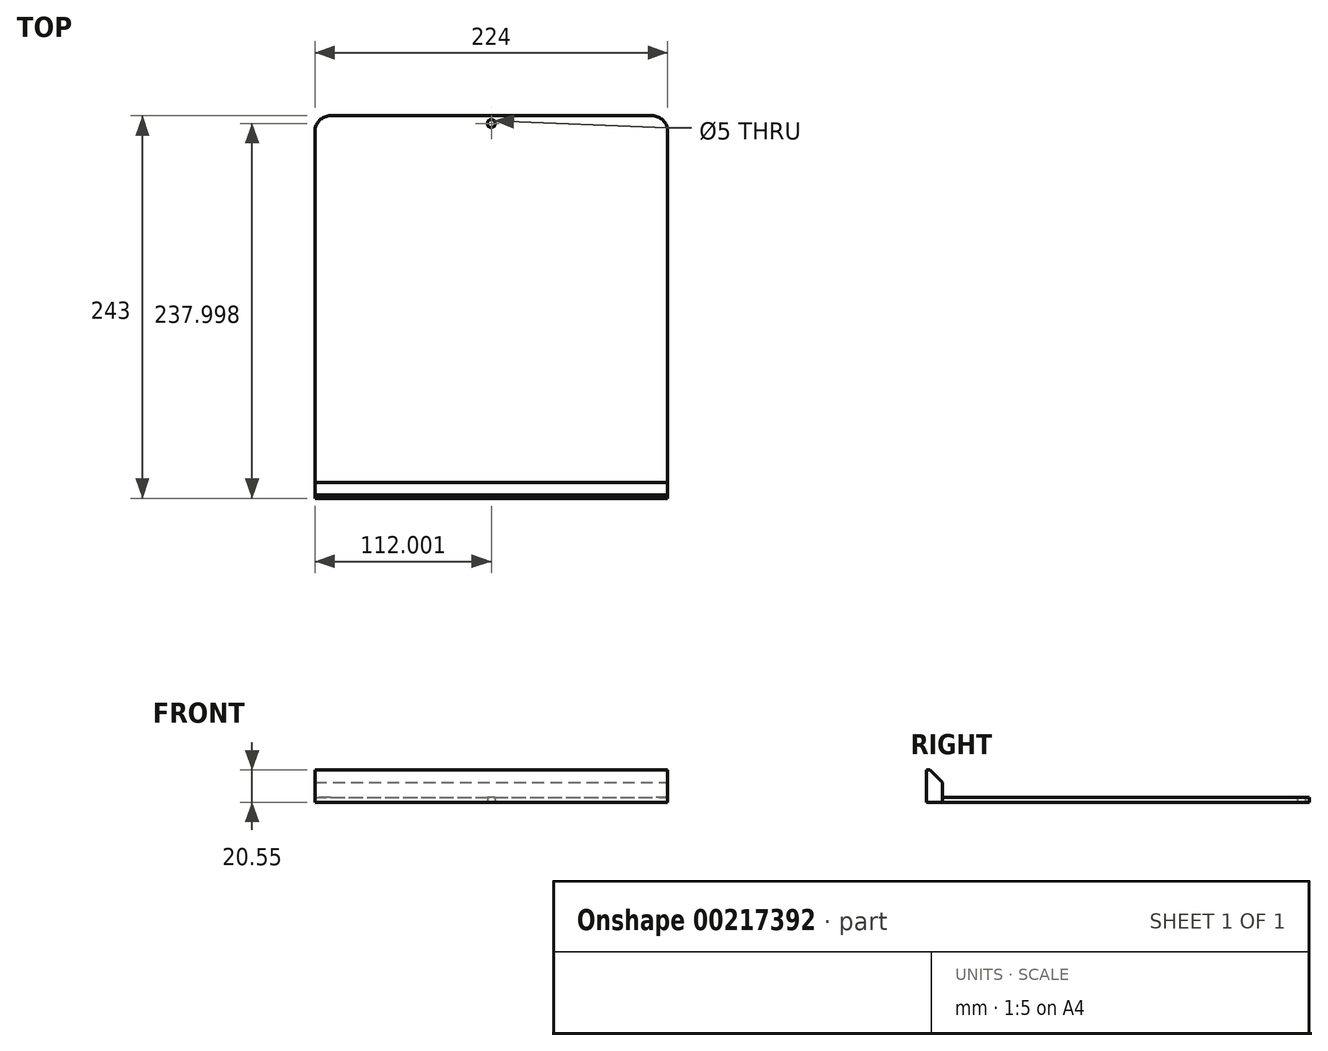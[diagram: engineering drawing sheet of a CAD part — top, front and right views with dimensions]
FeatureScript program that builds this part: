
annotation { "Feature Type Name" : "Feature", "Feature Type Description" : "" }
export const myFeature = defineFeature(function(context is Context, id is Id, definition is map)
    precondition{}
    {
        {
            var Q0;
            Q0=qCreatedBy(makeId("Top.planeOp"),FACE);
            var sketch = newSketch(context, id + "F0", { "sketchPlane" : qUnion([Q0])});
            skLineSegment(sketch, "E0.bottom", {"start": v(-146.57, -160.81) * mm, "end": v(77.43, -160.81) * mm});
            skLineSegment(sketch, "E0.top", {"start": v(-146.57, 72.19) * mm, "end": v(77.43, 72.19) * mm});
            skLineSegment(sketch, "E0.left", {"start": v(-146.57, -160.81) * mm, "end": v(-146.57, 72.19) * mm});
            skLineSegment(sketch, "E0.right", {"start": v(77.43, -160.81) * mm, "end": v(77.43, 72.19) * mm});
            skCircle(sketch, "E1", {"center": v(-34.57, 67.19) * mm, "radius": 2.5 * mm});
            skSolve(sketch);
        }
        {
            var Q0;
            Q0=makeQuery(id+"F0.imprint","IMPRINT",FACE,{"disambiguationData":[TD([[makeQuery(id+"F0.imprint","IMPRINT",EDGE,{"derivedFrom":sQuery(id+"F0.wireOp",EDGE,"E0.bottom")}),1.0]])]});
            extrude(context, id + "F1", {"entities" : qUnion([Q0]), "depth" : 3 * mm});
        }
        {
            var Q0;
            Q0=makeQuery(id+"F1.opExtrude","SWEPT_FACE",FACE,{"disambiguationData":[OSD([sQuery(id+"F0.wireOp",EDGE,"E0.bottom")])]});
            var sketch = newSketch(context, id + "F2", { "sketchPlane" : qUnion([Q0])});
            skLineSegment(sketch, "E2.bottom", {"start": v(-146.57, 0) * mm, "end": v(77.33, 0) * mm});
            skLineSegment(sketch, "E2.top", {"start": v(-146.57, 20.55) * mm, "end": v(77.33, 20.55) * mm});
            skLineSegment(sketch, "E2.left", {"start": v(-146.57, 0) * mm, "end": v(-146.57, 20.55) * mm});
            skLineSegment(sketch, "E2.right", {"start": v(77.33, 0) * mm, "end": v(77.33, 20.55) * mm});
            skSolve(sketch);
        }
        {
            var Q0;
            Q0 = qSketchRegion(id + "F2", true);
            extrude(context, id + "F3", {"entities" : qUnion([Q0]), "operationType" : NewBodyOperationType.ADD, "depth" : 10 * mm});
        }
        {
            var Q0;
            Q0=makeQuery(id+"F3.opExtrude","CAP_EDGE",EDGE,{"disambiguationData":[OSD([sQuery(id+"F2.wireOp",EDGE,"E2.top")])],"isStart":true});
            chamfer(context, id + "F4", {"entities" : qUnion([Q0]), "width" : 8 * mm, "tangentPropagation" : true});
        }
        {
            var Q0;
            Q0=makeQuery(id+"F1.opExtrude","SWEPT_EDGE",EDGE,{"disambiguationData":[OSD([sQuery(id+"F0.wireOp",EDGE,"E0.top"),sQuery(id+"F0.wireOp",EDGE,"E0.left")])]});
            fillet(context, id + "F5", {"entities" : qUnion([Q0]), "radius" : 10 * mm, "tangentPropagation" : true, "allowEdgeOverflow" : false});
        }
        {
            var Q0;
            Q0=makeQuery(id+"F1.opExtrude","SWEPT_EDGE",EDGE,{"disambiguationData":[OSD([sQuery(id+"F0.wireOp",EDGE,"E0.top"),sQuery(id+"F0.wireOp",EDGE,"E0.right")])]});
            fillet(context, id + "F6", {"entities" : qUnion([Q0]), "radius" : 10 * mm, "tangentPropagation" : true, "allowEdgeOverflow" : false});
        }
    });
